# Revit family: 2M_Check Valve_UNIVAL_CHE-1001 - 15-100 mm
name_source: partatom
category: Pipe Accessories
revit_build: Autodesk Revit 2016 (Build: 20150220_1215(x64)
units: mm (PartAtom-declared; Revit-internal decimal feet)

## family parameters
Always vertical = Yes
Cut with Voids When Loaded = No
OmniClass Number = 23.65.55.14
OmniClass Title = Valves for Liquid Services
Part Type = Valve - Breaks Into
Round Connector Dimension = Use Diameter
Shared = No
Work Plane-Based = No

## types (9) — shared parameters
Body Material = Brass
Certifications = TSE, EAC, CE
Connection Type = Wafer
Description = Disk check valve
Description TR = Disk tipi çek vana
Disc Material = Stainless steel
Loss Method = Not Defined
Manufacturer = Giacomini Unival
Giacomini Unival
Giacomini Unival
Max. Working Temperature = 180°C
Pressure Rating = PN16
Spring Material = Stainless steel
Standard No = TS 1074
URL = http://www.unival.com.tr

## per-type parameters (varying)
| type | DN | L | L1 | Model | d | d1 |
| DN15 | 15 mm | 16 mm  [stored 0.0524934 ft] | 3 mm  [stored 0.00984252 ft] | CHE-1001X015 | 40 mm  [stored 0.131234 ft] | 37 mm |
| DN20 | 20 mm | 19 mm  [stored 0.062336 ft] | 4 mm  [stored 0.0131234 ft] | CHE-1001X020 | 47 mm  [stored 0.154199 ft] | 44 mm |
| DN25 | 25 mm | 22 mm  [stored 0.0721785 ft] | 4 mm  [stored 0.0131234 ft] | CHE-1001X025 | 56 mm  [stored 0.183727 ft] | 52 mm |
| DN32 | 32 mm | 28 mm  [stored 0.0918635 ft] | 6 mm  [stored 0.019685 ft] | CHE-1001X032 | 72 mm  [stored 0.23622 ft] | 67 mm |
| DN40 | 40 mm | 32 mm  [stored 0.104987 ft] | 6 mm  [stored 0.019685 ft] | CHE-1001X040 | 82 mm  [stored 0.269029 ft] | 76 mm  [stored 0.249344 ft] |
| DN50 | 50 mm | 40 mm  [stored 0.131234 ft] | 8 mm  [stored 0.0262467 ft] | CHE-1001X050 | 95 mm | 88 mm |
| DN65 | 65 mm | 46 mm  [stored 0.150919 ft] | 9 mm | CHE-1001X065 | 115 mm | 107 mm |
| DN80 | 80 mm | 50 mm  [stored 0.164042 ft] | 10 mm  [stored 0.0328084 ft] | CHE-1001X080 | 132 mm | 123 mm |
| DN100 | 100 mm | 60 mm  [stored 0.19685 ft] | 12 mm  [stored 0.0393701 ft] | CHE-1001X100 | 152 mm | 141 mm |

note: [stored X ft] marks values corroborated as IEEE doubles in the binary element streams (Revit-internal decimal feet)

## geometry (parser evidence)
native form markers: Sweep x2
no freeform markers — native parametric forms only
